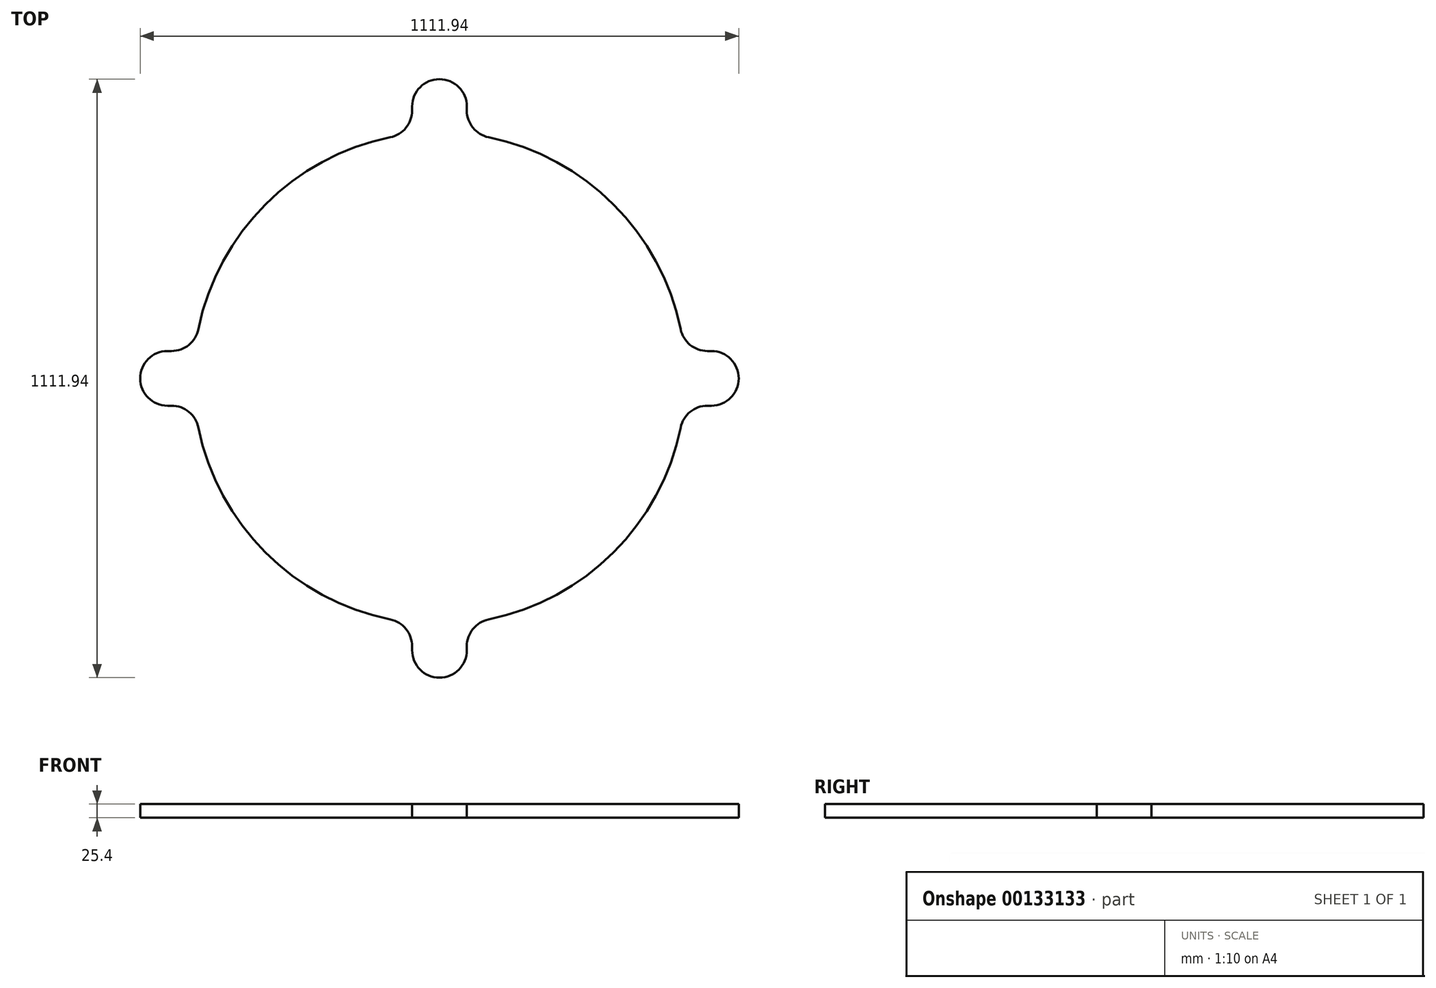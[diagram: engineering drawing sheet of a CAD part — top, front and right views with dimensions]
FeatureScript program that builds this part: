
annotation { "Feature Type Name" : "Feature", "Feature Type Description" : "" }
export const myFeature = defineFeature(function(context is Context, id is Id, definition is map)
    precondition{}
    {
        {
            var Q0;
            Q0=qCreatedBy(makeId("Top.planeOp"),FACE);
            var sketch = newSketch(context, id + "F0", { "sketchPlane" : qUnion([Q0])});
            skArc(sketch, "E0", {"start": v(-50.8, 454.37) * mm, "mid": v(-323.29, 323.29) * mm, "end": v(-454.37, 50.8) * mm});
            skLineSegment(sketch, "E1.bottom", {"start": v(454.37, -50.8) * mm, "end": v(555.97, -50.8) * mm});
            skLineSegment(sketch, "E1.top", {"start": v(454.37, 50.8) * mm, "end": v(555.97, 50.8) * mm});
            skLineSegment(sketch, "E1.left", {"start": v(454.37, -50.8) * mm, "end": v(454.37, 50.8) * mm, "construction": true});
            skLineSegment(sketch, "E1.right", {"start": v(555.97, -50.8) * mm, "end": v(555.97, 50.8) * mm});
            skLineSegment(sketch, "E2", {"start": v(-457.2, 0) * mm, "end": v(457.2, 0) * mm, "construction": true});
            skPoint(sketch, "E2.endSnap0", {"position": v(454.37, 0) * mm});
            skLineSegment(sketch, "E3", {"start": v(0, -457.2) * mm, "end": v(0, 457.2) * mm, "construction": true});
            skLineSegment(sketch, "E4.bottom", {"start": v(-50.8, 454.37) * mm, "end": v(50.8, 454.37) * mm, "construction": true});
            skLineSegment(sketch, "E4.top", {"start": v(-50.8, 555.97) * mm, "end": v(50.8, 555.97) * mm});
            skLineSegment(sketch, "E4.left", {"start": v(-50.8, 454.37) * mm, "end": v(-50.8, 555.97) * mm});
            skLineSegment(sketch, "E4.right", {"start": v(50.8, 454.37) * mm, "end": v(50.8, 555.97) * mm});
            skLineSegment(sketch, "E5.bottom", {"start": v(-50.8, -454.37) * mm, "end": v(50.8, -454.37) * mm, "construction": true});
            skLineSegment(sketch, "E5.top", {"start": v(-50.8, -555.97) * mm, "end": v(50.8, -555.97) * mm});
            skLineSegment(sketch, "E5.left", {"start": v(-50.8, -454.37) * mm, "end": v(-50.8, -555.97) * mm});
            skLineSegment(sketch, "E5.right", {"start": v(50.8, -454.37) * mm, "end": v(50.8, -555.97) * mm});
            skLineSegment(sketch, "E6.bottom", {"start": v(-454.37, -50.8) * mm, "end": v(-555.97, -50.8) * mm});
            skLineSegment(sketch, "E6.top", {"start": v(-454.37, 50.8) * mm, "end": v(-555.97, 50.8) * mm});
            skLineSegment(sketch, "E6.left", {"start": v(-454.37, -50.8) * mm, "end": v(-454.37, 50.8) * mm, "construction": true});
            skLineSegment(sketch, "E6.right", {"start": v(-555.97, -50.8) * mm, "end": v(-555.97, 50.8) * mm});
            skArc(sketch, "E7.trimOffspring", {"start": v(454.37, 50.8) * mm, "mid": v(323.29, 323.29) * mm, "end": v(50.8, 454.37) * mm});
            skArc(sketch, "E8.trimOffspring", {"start": v(50.8, -454.37) * mm, "mid": v(323.29, -323.29) * mm, "end": v(454.37, -50.8) * mm});
            skArc(sketch, "E9.trimOffspring", {"start": v(-454.37, -50.8) * mm, "mid": v(-323.29, -323.29) * mm, "end": v(-50.8, -454.37) * mm});
            skLineSegment(sketch, "E10", {"start": v(454.37, 50.8) * mm, "end": v(555.97, -50.8) * mm, "construction": true});
            skLineSegment(sketch, "E11", {"start": v(555.97, 50.8) * mm, "end": v(454.37, -50.8) * mm, "construction": true});
            skLineSegment(sketch, "E12", {"start": v(-50.8, 555.97) * mm, "end": v(50.8, 454.37) * mm, "construction": true});
            skLineSegment(sketch, "E13", {"start": v(-50.8, 454.37) * mm, "end": v(50.8, 555.97) * mm, "construction": true});
            skLineSegment(sketch, "E14", {"start": v(-555.97, 50.8) * mm, "end": v(-454.37, -50.8) * mm, "construction": true});
            skLineSegment(sketch, "E15", {"start": v(-454.37, 50.8) * mm, "end": v(-555.97, -50.8) * mm, "construction": true});
            skLineSegment(sketch, "E16", {"start": v(50.8, -555.97) * mm, "end": v(-50.8, -454.37) * mm, "construction": true});
            skLineSegment(sketch, "E17", {"start": v(-50.8, -555.97) * mm, "end": v(50.8, -454.37) * mm, "construction": true});
            skSolve(sketch);
        }
        {
            var Q0;
            Q0=qSketchRegion(id+"F0",true);
            extrude(context, id + "F1", {"entities" : qUnion([Q0]), "depth" : 25.4 * mm});
        }
        {
            var Q0;
            Q0=makeQuery(id+"F1.opExtrude","SWEPT_EDGE",EDGE,{"disambiguationData":[OSD([sQuery(id+"F0.wireOp",EDGE,"E5.top"),sQuery(id+"F0.wireOp",EDGE,"E5.right")])]});
            var Q1;
            Q1=makeQuery(id+"F1.opExtrude","SWEPT_EDGE",EDGE,{"disambiguationData":[OSD([sQuery(id+"F0.wireOp",EDGE,"E5.top"),sQuery(id+"F0.wireOp",EDGE,"E5.left")])]});
            var Q2;
            Q2=makeQuery(id+"F1.opExtrude","SWEPT_EDGE",EDGE,{"disambiguationData":[OSD([sQuery(id+"F0.wireOp",EDGE,"E1.bottom"),sQuery(id+"F0.wireOp",EDGE,"E1.right")])]});
            var Q3;
            Q3=makeQuery(id+"F1.opExtrude","SWEPT_EDGE",EDGE,{"disambiguationData":[OSD([sQuery(id+"F0.wireOp",EDGE,"E1.top"),sQuery(id+"F0.wireOp",EDGE,"E1.right")])]});
            var Q4;
            Q4=makeQuery(id+"F1.opExtrude","SWEPT_EDGE",EDGE,{"disambiguationData":[OSD([sQuery(id+"F0.wireOp",EDGE,"E4.top"),sQuery(id+"F0.wireOp",EDGE,"E4.right")])]});
            var Q5;
            Q5=makeQuery(id+"F1.opExtrude","SWEPT_EDGE",EDGE,{"disambiguationData":[OSD([sQuery(id+"F0.wireOp",EDGE,"E4.top"),sQuery(id+"F0.wireOp",EDGE,"E4.left")])]});
            var Q6;
            Q6=makeQuery(id+"F1.opExtrude","SWEPT_EDGE",EDGE,{"disambiguationData":[OSD([sQuery(id+"F0.wireOp",EDGE,"E6.top"),sQuery(id+"F0.wireOp",EDGE,"E6.right")])]});
            var Q7;
            Q7=makeQuery(id+"F1.opExtrude","SWEPT_EDGE",EDGE,{"disambiguationData":[OSD([sQuery(id+"F0.wireOp",EDGE,"E6.bottom"),sQuery(id+"F0.wireOp",EDGE,"E6.right")])]});
            var Q8;
            Q8=makeQuery(id+"F1.opExtrude","SWEPT_EDGE",EDGE,{"disambiguationData":[OSD([sQuery(id+"F0.wireOp",EDGE,"E5.right"),sQuery(id+"F0.wireOp",EDGE,"E8.trimOffspring")])]});
            var Q9;
            Q9=makeQuery(id+"F1.opExtrude","SWEPT_EDGE",EDGE,{"disambiguationData":[OSD([sQuery(id+"F0.wireOp",EDGE,"E1.bottom"),sQuery(id+"F0.wireOp",EDGE,"E8.trimOffspring")])]});
            var Q10;
            Q10=makeQuery(id+"F1.opExtrude","SWEPT_EDGE",EDGE,{"disambiguationData":[OSD([sQuery(id+"F0.wireOp",EDGE,"E1.top"),sQuery(id+"F0.wireOp",EDGE,"E7.trimOffspring")])]});
            var Q11;
            Q11=makeQuery(id+"F1.opExtrude","SWEPT_EDGE",EDGE,{"disambiguationData":[OSD([sQuery(id+"F0.wireOp",EDGE,"E4.right"),sQuery(id+"F0.wireOp",EDGE,"E7.trimOffspring")])]});
            var Q12;
            Q12=makeQuery(id+"F1.opExtrude","SWEPT_EDGE",EDGE,{"disambiguationData":[OSD([sQuery(id+"F0.wireOp",EDGE,"E0"),sQuery(id+"F0.wireOp",EDGE,"E4.left")])]});
            var Q13;
            Q13=makeQuery(id+"F1.opExtrude","SWEPT_EDGE",EDGE,{"disambiguationData":[OSD([sQuery(id+"F0.wireOp",EDGE,"E0"),sQuery(id+"F0.wireOp",EDGE,"E6.top")])]});
            var Q14;
            Q14=makeQuery(id+"F1.opExtrude","SWEPT_EDGE",EDGE,{"disambiguationData":[OSD([sQuery(id+"F0.wireOp",EDGE,"E6.bottom"),sQuery(id+"F0.wireOp",EDGE,"E9.trimOffspring")])]});
            var Q15;
            Q15=makeQuery(id+"F1.opExtrude","SWEPT_EDGE",EDGE,{"disambiguationData":[OSD([sQuery(id+"F0.wireOp",EDGE,"E5.left"),sQuery(id+"F0.wireOp",EDGE,"E9.trimOffspring")])]});
            fillet(context, id + "F2", {"entities" : qUnion([Q0, Q1, Q2, Q3, Q4, Q5, Q6, Q7, Q8, Q9, Q10, Q11, Q12, Q13, Q14, Q15]), "radius" : 50.8 * mm, "tangentPropagation" : true, "allowEdgeOverflow" : false});
        }
    });
